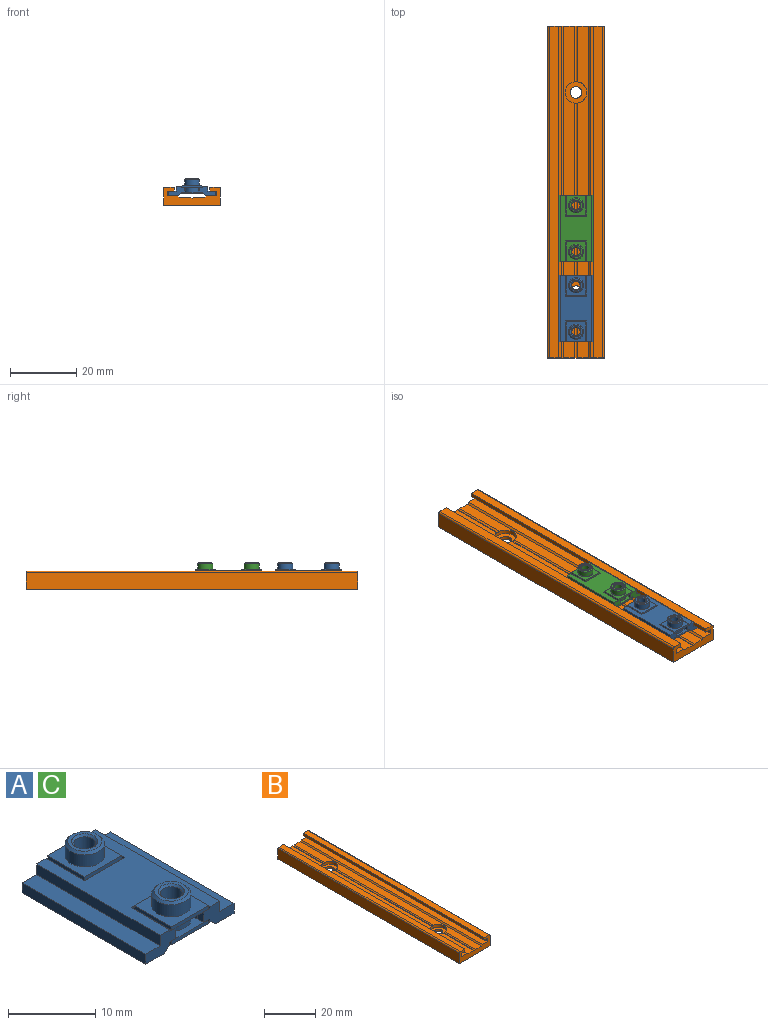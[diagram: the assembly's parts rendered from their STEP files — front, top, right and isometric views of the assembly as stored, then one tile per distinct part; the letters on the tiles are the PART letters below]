
ASSEMBLY  parts=3 mates=2
PART A: 78 faces, bbox 14.3x20x5.2 mm
  f0: cone r=2.1mm half-angle=45deg, axis (0,0,-1), area 5.6mm2, adj f1,f33
  f1: cylinder r=2.25mm len=4.5mm, axis (0,0,-1), area 24mm2, adj f0,f26
  f2: cone r=1.38mm half-angle=45deg, axis (0,0,-1), area 3.1mm2, adj f3,f34
  f3: cylinder r=1.25mm len=4mm, axis (0,0,-1), area 31.4mm2, adj f2,f4
  f4: cone r=1.38mm half-angle=45deg, axis (0,0,1), area 3.1mm2, adj f3,f33
  f5: cone r=2.1mm half-angle=45deg, axis (0,0,-1), area 5.6mm2, adj f6,f18
  f6: cylinder r=2.25mm len=4.5mm, axis (0,0,-1), area 24mm2, adj f5,f13
  f7: cone r=1.38mm half-angle=45deg, axis (0,0,-1), area 3.1mm2, adj f8,f19
  f8: cylinder r=1.25mm len=4mm, axis (0,0,-1), area 31.4mm2, adj f7,f9
  f9: cone r=1.38mm half-angle=45deg, axis (0,0,1), area 3.1mm2, adj f8,f18
  f10: plane 4.5x1.96mm, normal (0,0,-1), area 5.1mm2, adj f11,f16,f51,f52,f57,f58
  f11: cylinder r=2.25mm len=3.99mm, axis (0,0,-1), area 7.3mm2, adj f10,f12,f51,f57
  f12: plane 4.5x1.96mm, normal (0,0,1), area 5.1mm2, adj f11,f22,f51,f52,f57,f58
  f13: plane 6x6mm, normal (0,0,1), area 20.1mm2, adj f6,f14,f15,f16,f17
  f14: plane 6x0.5mm, normal (0,-1,0), area 3mm2, adj f13,f15,f17,f24
  f15: plane 6x0.5mm, normal (-1,0,0), area 3mm2, adj f13,f14,f16,f24
  f16: plane 6x0.5mm, normal (0,1,0), area 3mm2, adj f10,f13,f15,f17,f53,f66
  f17: plane 6x0.5mm, normal (1,0,0), area 3mm2, adj f13,f14,f16,f24
  f18: plane 3.9x3.9mm, normal (0,0,1), area 4.9mm2, adj f5,f9
  f19: plane 6x6mm, normal (0,0,-1), area 28.9mm2, adj f7,f20,f21,f22,f23
  f20: plane 6x0.5mm, normal (0,-1,0), area 3mm2, adj f19,f21,f23,f47
  f21: plane 6x0.5mm, normal (-1,0,0), area 3mm2, adj f19,f20,f22,f47
  f22: plane 6x0.5mm, normal (0,1,0), area 3mm2, adj f12,f19,f21,f23,f53,f66
  f23: plane 6x0.5mm, normal (1,0,0), area 3mm2, adj f19,f20,f22,f47
  f24: plane 6.5x6.25mm, normal (0,0,1), area 4.6mm2, adj f14,f15,f17,f53,f63,f64,f65,f66
  f25: plane 4.5x1.96mm, normal (0,0,1), area 5.1mm2, adj f32,f35,f43,f44,f54,f55
  f26: plane 6x6mm, normal (0,0,1), area 20.1mm2, adj f1,f28,f29,f30,f31
  f27: plane 4.5x1.96mm, normal (0,0,-1), area 5.1mm2, adj f28,f32,f43,f44,f54,f55
  f28: plane 6x0.5mm, normal (0,-1,0), area 3mm2, adj f26,f27,f29,f31,f45,f56
  f29: plane 6x0.5mm, normal (-1,0,0), area 3mm2, adj f26,f28,f30,f59
  f30: plane 6x0.5mm, normal (0,1,0), area 3mm2, adj f26,f29,f31,f59
  f31: plane 6x0.5mm, normal (1,0,0), area 3mm2, adj f26,f28,f30,f59
  f32: cylinder r=2.25mm len=3.99mm, axis (0,0,-1), area 7.3mm2, adj f25,f27,f43,f55
  f33: plane 3.9x3.9mm, normal (0,0,1), area 4.9mm2, adj f0,f4
  f34: plane 6x6mm, normal (0,0,-1), area 28.9mm2, adj f2,f35,f36,f37,f38
  f35: plane 6x0.5mm, normal (0,-1,0), area 3mm2, adj f25,f34,f36,f38,f45,f56
  f36: plane 6x0.5mm, normal (-1,0,0), area 3mm2, adj f34,f35,f37,f39
  f37: plane 6x0.5mm, normal (0,1,0), area 3mm2, adj f34,f36,f38,f39
  f38: plane 6x0.5mm, normal (1,0,0), area 3mm2, adj f34,f35,f37,f39
  f39: plane 6.5x6.25mm, normal (0,0,-1), area 4.6mm2, adj f36,f37,f38,f40,f41,f42,f45,f56
  f40: plane 6.25x0.45mm, normal (-1,0,0), area 2.8mm2, adj f39,f41,f45,f46
  f41: plane 6.5x0.45mm, normal (0,-1,0), area 2.9mm2, adj f39,f40,f42,f46
  f42: plane 6.25x0.45mm, normal (1,0,0), area 2.8mm2, adj f39,f41,f46,f56
  f43: plane 1.5x0.96mm, normal (-0.97,-0.26,0), area 1.5mm2, adj f25,f27,f32,f44
  f44: plane 1.5x1mm, normal (-1,0,0), area 1.5mm2, adj f25,f27,f43,f45
  f45: plane 4.9x2.88mm, normal (0,-1,0), area 8.9mm2, adj f28,f35,f39,f40,f44,f46,f59,f62
  f46: plane 20x6.9mm, normal (0,0,-1), area 56.7mm2, adj f40,f41,f42,f45,f48,f49,f50,f53
  f47: plane 6.5x6.25mm, normal (0,0,-1), area 4.6mm2, adj f20,f21,f23,f48,f49,f50,f53,f66
  f48: plane 6.25x0.45mm, normal (1,0,0), area 2.8mm2, adj f46,f47,f49,f53
  f49: plane 6.5x0.45mm, normal (0,1,0), area 2.9mm2, adj f46,f47,f48,f50
  f50: plane 6.25x0.45mm, normal (-1,0,0), area 2.8mm2, adj f46,f47,f49,f66
  f51: plane 1.5x0.96mm, normal (0.97,0.26,0), area 1.5mm2, adj f10,f11,f12,f52
  f52: plane 1.5x1mm, normal (1,0,0), area 1.5mm2, adj f10,f12,f51,f53
  f53: plane 4.9x2.88mm, normal (0,1,0), area 8.9mm2, adj f16,f22,f24,f46,f47,f48,f52,f65
  f54: plane 1.5x1mm, normal (1,0,0), area 1.5mm2, adj f25,f27,f55,f56
  f55: plane 1.5x0.96mm, normal (0.97,-0.26,0), area 1.5mm2, adj f25,f27,f32,f54
  f56: plane 4.9x2.88mm, normal (0,-1,0), area 8.9mm2, adj f28,f35,f39,f42,f46,f54,f59,f60
  f57: plane 1.5x0.96mm, normal (-0.97,0.26,0), area 1.5mm2, adj f10,f11,f12,f58
  f58: plane 1.5x1mm, normal (-1,0,0), area 1.5mm2, adj f10,f12,f57,f66
  f59: plane 6.5x6.25mm, normal (0,0,1), area 4.6mm2, adj f29,f30,f31,f45,f56,f60,f61,f62
  f60: plane 6.25x0.23mm, normal (1,0,0), area 1.4mm2, adj f56,f59,f61,f69
  f61: plane 6.5x0.23mm, normal (0,-1,0), area 1.5mm2, adj f59,f60,f62,f69
  f62: plane 6.25x0.23mm, normal (-1,0,0), area 1.4mm2, adj f45,f59,f61,f69
  f63: plane 6.25x0.23mm, normal (-1,0,0), area 1.4mm2, adj f24,f64,f66,f69
  f64: plane 6.5x0.23mm, normal (0,1,0), area 1.5mm2, adj f24,f63,f65,f69
  f65: plane 6.25x0.23mm, normal (1,0,0), area 1.4mm2, adj f24,f53,f64,f69
  f66: plane 4.9x2.88mm, normal (0,1,0), area 8.9mm2, adj f16,f22,f24,f46,f47,f50,f58,f63
  f67: plane 20x2.35mm, normal (0,0,1), area 47mm2, adj f45,f66,f68,f77
  f68: plane 20x1.48mm, normal (1,0,0), area 29.6mm2, adj f45,f66,f67,f69
  f69: plane 20x9.6mm, normal (0,0,1), area 110.7mm2, adj f45,f53,f56,f60,f61,f62,f63,f64
  f70: plane 20x1.48mm, normal (-1,0,0), area 29.6mm2, adj f53,f56,f69,f71
  f71: plane 20x2.35mm, normal (0,0,1), area 47mm2, adj f53,f56,f70,f72
  f72: plane 20x1.4mm, normal (-1,0,0), area 28mm2, adj f53,f56,f71,f73
  f73: plane 20x3mm, normal (0,0,-1), area 60mm2, adj f53,f56,f72,f74
  f74: plane 20x0.7mm, normal (0.71,0,-0.71), area 19.8mm2, adj f46,f53,f56,f73
  f75: plane 20x0.7mm, normal (-0.71,0,-0.71), area 19.8mm2, adj f45,f46,f66,f76
  f76: plane 20x3mm, normal (0,0,-1), area 60mm2, adj f45,f66,f75,f77
  f77: plane 20x1.4mm, normal (1,0,0), area 28mm2, adj f45,f66,f67,f76
PART B: 33 faces, bbox 17x100x5.5 mm
  f0: cylinder r=3.25mm len=6.5mm, axis (0,0,-1), area 26.3mm2, adj f5,f6,f7,f8,f9,f21,f22
  f1: cylinder r=1.75mm len=3.5mm, axis (0,0,-1), area 11mm2, adj f8,f12
  f2: cylinder r=3.25mm len=6.5mm, axis (0,0,-1), area 26.3mm2, adj f4,f5,f6,f7,f9,f10,f11
  f3: cylinder r=1.75mm len=3.5mm, axis (0,0,-1), area 11mm2, adj f4,f12
  f4: plane 6.5x6.5mm, normal (0,0,1), area 23.6mm2, adj f2,f3
  f5: plane 100x3.25mm, normal (0,0,1), area 298.3mm2, adj f0,f2,f6,f11,f20,f21,f31,f32
  f6: plane 53.58x0.5mm, normal (-0.5,0,0.87), area 30.9mm2, adj f0,f2,f5,f7
  f7: plane 53.58x0.5mm, normal (0.5,0,0.87), area 30.9mm2, adj f0,f2,f6,f9
  f8: plane 6.5x6.5mm, normal (0,0,1), area 23.6mm2, adj f0,f1
  f9: plane 100x3.25mm, normal (0,0,1), area 298.3mm2, adj f0,f2,f7,f10,f22,f23,f31,f32
  f10: plane 16.79x0.5mm, normal (0.5,0,0.87), area 9.7mm2, adj f2,f9,f11,f31
  f11: plane 16.79x0.5mm, normal (-0.5,0,0.87), area 9.7mm2, adj f2,f5,f10,f31
  f12: plane 100x17mm, normal (0,0,-1), area 1680.8mm2, adj f1,f3,f13,f30,f31,f32
  f13: plane 100x5mm, normal (1,0,0), area 500mm2, adj f12,f14,f31,f32
  f14: cylinder r=0.5mm len=100mm, axis (0,-1,0), area 78.5mm2, adj f13,f15,f31,f32
  f15: plane 100x2.7mm, normal (0,0,1), area 270mm2, adj f14,f16,f31,f32
  f16: plane 100x1.2mm, normal (-1,0,0), area 120mm2, adj f15,f17,f31,f32
  f17: plane 100x2mm, normal (0,0,-1), area 200mm2, adj f16,f18,f31,f32
  f18: plane 100x1.5mm, normal (-1,0,0), area 150mm2, adj f17,f19,f31,f32
  f19: plane 100x3.05mm, normal (0,0,1), area 305mm2, adj f18,f20,f31,f32
  f20: plane 100x0.5mm, normal (-0.71,0,0.71), area 70.7mm2, adj f5,f19,f31,f32
  f21: plane 16.79x0.5mm, normal (-0.5,0,0.87), area 9.7mm2, adj f0,f5,f22,f32
  f22: plane 16.79x0.5mm, normal (0.5,0,0.87), area 9.7mm2, adj f0,f9,f21,f32
  f23: plane 100x0.5mm, normal (0.71,0,0.71), area 70.7mm2, adj f9,f24,f31,f32
  f24: plane 100x3.05mm, normal (0,0,1), area 305mm2, adj f23,f25,f31,f32
  f25: plane 100x1.5mm, normal (1,0,0), area 150mm2, adj f24,f26,f31,f32
  f26: plane 100x2mm, normal (0,0,-1), area 200mm2, adj f25,f27,f31,f32
  f27: plane 100x1.2mm, normal (1,0,0), area 120mm2, adj f26,f28,f31,f32
  f28: plane 100x2.7mm, normal (0,0,1), area 270mm2, adj f27,f29,f31,f32
  f29: cylinder r=0.5mm len=100mm, axis (0,-1,0), area 78.5mm2, adj f28,f30,f31,f32
  f30: plane 100x5mm, normal (-1,0,0), area 500mm2, adj f12,f29,f31,f32
  f31: plane 17x5.5mm, normal (0,1,0), area 54.6mm2, adj f5,f9,f10,f11,f12,f13,f14,f15
  f32: plane 17x5.5mm, normal (0,-1,0), area 54.6mm2, adj f5,f9,f12,f13,f14,f15,f16,f17
PART C: same geometry as A
PLACE A t=(4.61,-21,25.34)mm
PLACE B t=(4.61,-35.88,25.34)mm fixed
PLACE C t=(4.61,3.1,25.34)mm
MATE slider C.f35 <-> B.f32  axis (0,1,0) through (4.61,-6.9,28.19)mm
MATE slider A.f35 <-> B.f32  axis (0,1,0) through (4.61,-31,28.19)mm
